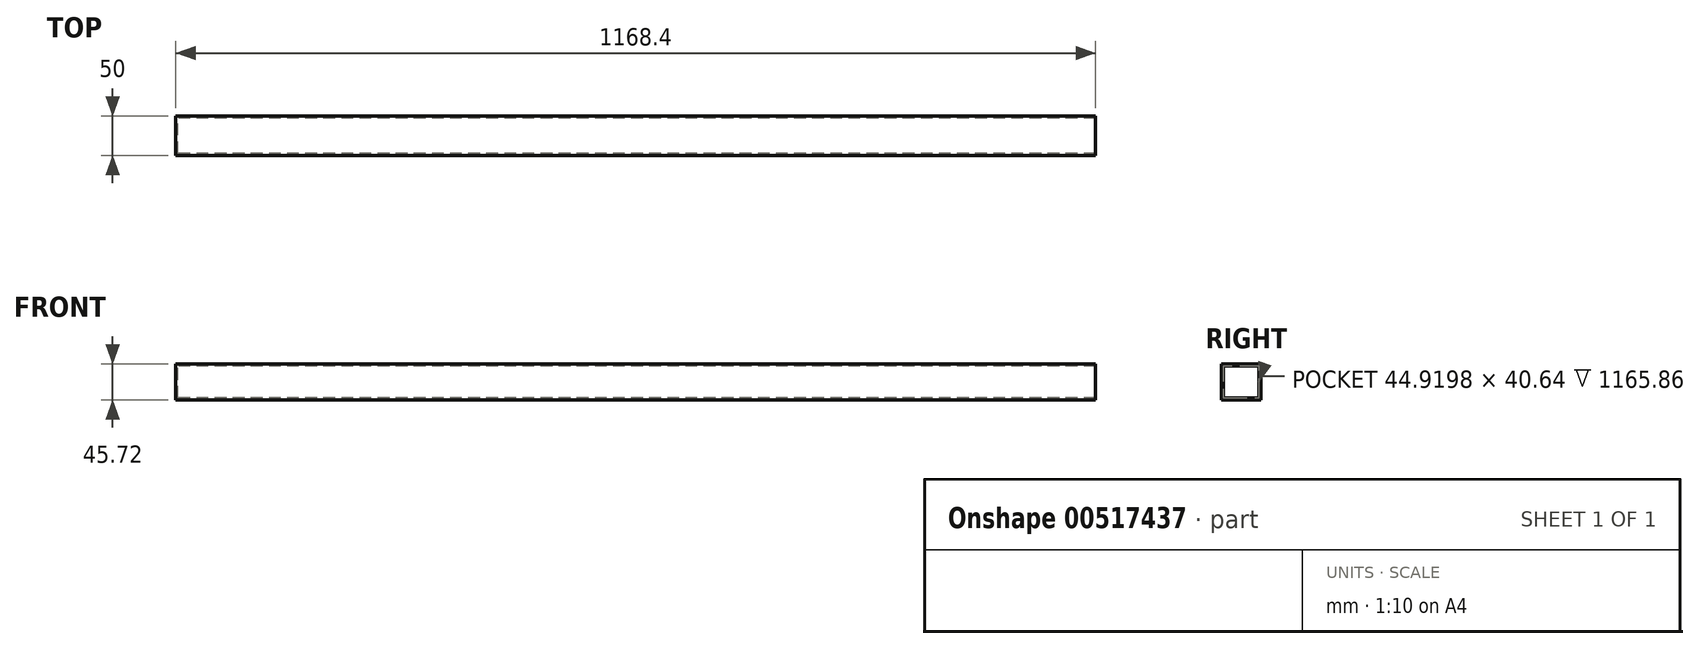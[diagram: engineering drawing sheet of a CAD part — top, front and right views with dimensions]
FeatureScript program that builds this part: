
annotation { "Feature Type Name" : "Feature", "Feature Type Description" : "" }
export const myFeature = defineFeature(function(context is Context, id is Id, definition is map)
    precondition{}
    {
        {
            var Q0;
            Q0=qCreatedBy(makeId("Right.planeOp"),FACE);
            var sketch = newSketch(context, id + "F0", { "sketchPlane" : qUnion([Q0])});
            skLineSegment(sketch, "E0.bottom", {"start": v(-25, -22.86) * mm, "end": v(25, -22.86) * mm});
            skLineSegment(sketch, "E0.top", {"start": v(-25, 22.86) * mm, "end": v(25, 22.86) * mm});
            skLineSegment(sketch, "E0.left", {"start": v(-25, -22.86) * mm, "end": v(-25, 22.86) * mm});
            skLineSegment(sketch, "E0.right", {"start": v(25, -22.86) * mm, "end": v(25, 22.86) * mm});
            skPoint(sketch, "E0.middle", {"position": v(0, 0) * mm});
            skSolve(sketch);
        }
        {
            var Q0;
            Q0 = qSketchRegion(id + "F0", true);
            extrude(context, id + "F1", {"entities" : qUnion([Q0]), "depth" : 1168.4 * mm, "offsetDistance" : 25.4 * mm});
        }
        {
            var Q0;
            Q0=makeQuery(id+"F1.opExtrude","CAP_FACE",FACE,{"disambiguationData":[OSD([sQuery(id+"F0.wireOp",EDGE,"E0.bottom"),sQuery(id+"F0.wireOp",EDGE,"E0.top"),sQuery(id+"F0.wireOp",EDGE,"E0.left"),sQuery(id+"F0.wireOp",EDGE,"E0.right")])],"isStart":false});
            shell(context, id + "F2", {"entities" : qUnion([Q0]), "thickness" : 2.54 * mm});
        }
    });
